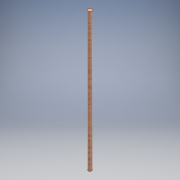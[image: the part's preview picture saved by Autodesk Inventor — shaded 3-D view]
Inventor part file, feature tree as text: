
AUTODESK INVENTOR PART (.ipt)
format: ipt  version: 2018 (Build 220112000, 112)  size: 92,672 bytes
history: native  units: mm
features: other x1, extrude x1, sketch x1
ambient origin geometry x8: Origin, YZ Plane, XZ Plane, XY Plane, X Axis, Y Axis, Z Axis, Center Point
bodies: Body1 (feature_tree)
feature tree (3):
  other  "ソリッド1"
  extrude  "押し出し1"  Depth=6.0mm
  sketch  "スケッチ1"
